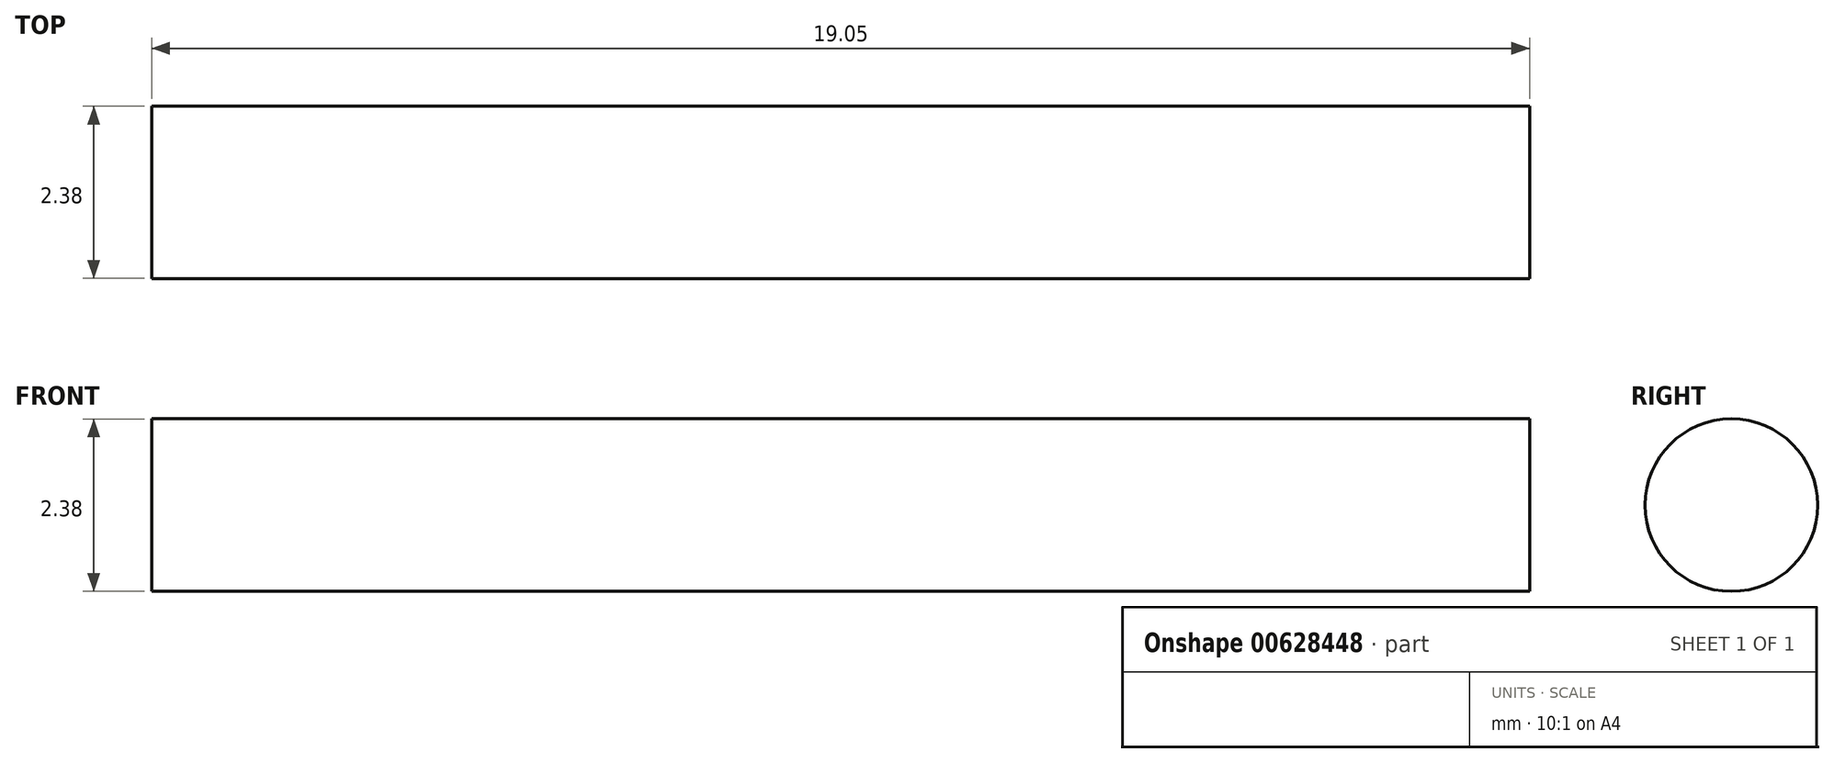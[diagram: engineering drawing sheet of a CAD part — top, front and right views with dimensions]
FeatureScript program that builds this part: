
annotation { "Feature Type Name" : "Feature", "Feature Type Description" : "" }
export const myFeature = defineFeature(function(context is Context, id is Id, definition is map)
    precondition{}
    {
        {
            var Q0;
            Q0=qCreatedBy(makeId("Right.planeOp"),FACE);
            var sketch = newSketch(context, id + "F0", { "sketchPlane" : qUnion([Q0])});
            skCircle(sketch, "E0", {"center": v(0, 0) * mm, "radius": 1.2 * mm});
            skSolve(sketch);
        }
        {
            var Q0;
            Q0 = qSketchRegion(id + "F0", true);
            extrude(context, id + "F1", {"entities" : qUnion([Q0]), "oppositeDirection" : true, "depth" : 19.05 * mm, "offsetDistance" : 25.4 * mm});
        }
    });
